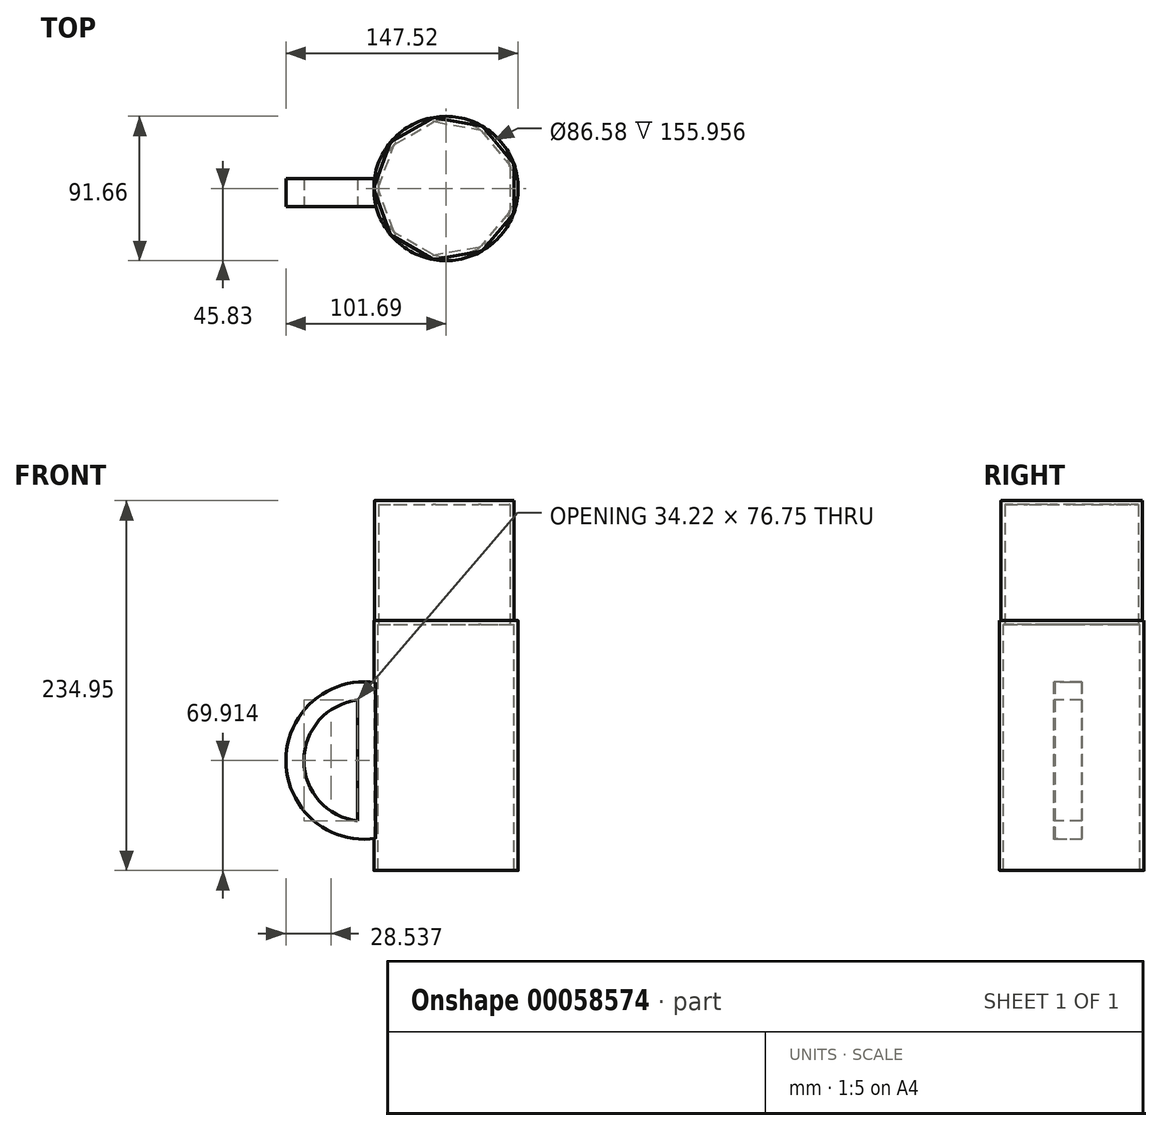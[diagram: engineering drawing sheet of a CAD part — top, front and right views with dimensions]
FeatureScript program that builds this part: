
annotation { "Feature Type Name" : "Feature", "Feature Type Description" : "" }
export const myFeature = defineFeature(function(context is Context, id is Id, definition is map)
    precondition{}
    {
        {
            var Q0;
            Q0=qCreatedBy(makeId("Top.planeOp"),FACE);
            var sketch = newSketch(context, id + "F0", { "sketchPlane" : qUnion([Q0])});
            skCircle(sketch, "E0.cCircle", {"center": v(0, 0) * mm, "radius": 43.07 * mm, "construction": true});
            skLineSegment(sketch, "E0.0", {"start": v(43.07, 15.68) * mm, "end": v(43.07, -15.68) * mm});
            skLineSegment(sketch, "E0.1", {"start": v(43.07, -15.68) * mm, "end": v(22.92, -39.7) * mm});
            skLineSegment(sketch, "E0.2", {"start": v(22.92, -39.7) * mm, "end": v(-7.96, -45.14) * mm});
            skLineSegment(sketch, "E0.3", {"start": v(-7.96, -45.14) * mm, "end": v(-35.1, -29.46) * mm});
            skLineSegment(sketch, "E0.4", {"start": v(-35.1, -29.46) * mm, "end": v(-45.83, 0) * mm});
            skLineSegment(sketch, "E0.5", {"start": v(-45.83, 0) * mm, "end": v(-35.1, 29.46) * mm});
            skLineSegment(sketch, "E0.6", {"start": v(-35.1, 29.46) * mm, "end": v(-7.96, 45.14) * mm});
            skLineSegment(sketch, "E0.7", {"start": v(-7.96, 45.14) * mm, "end": v(22.92, 39.7) * mm});
            skLineSegment(sketch, "E0.8", {"start": v(22.92, 39.7) * mm, "end": v(43.07, 15.68) * mm});
            skPoint(sketch, "E0.0.midPoint", {"position": v(43.07, 0) * mm});
            skSolve(sketch);
        }
        {
            var Q0;
            Q0 = qSketchRegion(id + "F0", true);
            extrude(context, id + "F1", {"entities" : qUnion([Q0]), "depth" : 76.2 * mm});
        }
        {
            var Q0;
            Q0=makeQuery(id+"F1.opExtrude","CAP_FACE",FACE,{"disambiguationData":[OSD([sQuery(id+"F0.wireOp",EDGE,"E0.0"),sQuery(id+"F0.wireOp",EDGE,"E0.1"),sQuery(id+"F0.wireOp",EDGE,"E0.2"),sQuery(id+"F0.wireOp",EDGE,"E0.3"),sQuery(id+"F0.wireOp",EDGE,"E0.4"),sQuery(id+"F0.wireOp",EDGE,"E0.5"),sQuery(id+"F0.wireOp",EDGE,"E0.6"),sQuery(id+"F0.wireOp",EDGE,"E0.7"),sQuery(id+"F0.wireOp",EDGE,"E0.8")])],"isStart":true});
            var sketch = newSketch(context, id + "F2", { "sketchPlane" : qUnion([Q0])});
            skCircle(sketch, "E1", {"center": v(0, 0) * mm, "radius": 45.83 * mm});
            skSolve(sketch);
        }
        {
            var Q0;
            Q0 = qSketchRegion(id + "F2", true);
            extrude(context, id + "F3", {"entities" : qUnion([Q0]), "operationType" : NewBodyOperationType.ADD, "depth" : 158.75 * mm});
        }
        {
            var Q0;
            Q0=makeQuery(id+"F1.opExtrude","SWEPT_EDGE",EDGE,{"disambiguationData":[OSD([sQuery(id+"F0.wireOp",EDGE,"E0.1"),sQuery(id+"F0.wireOp",EDGE,"E0.2")])]});
            var Q1;
            Q1=makeQuery(id+"F1.opExtrude","SWEPT_EDGE",EDGE,{"disambiguationData":[OSD([sQuery(id+"F0.wireOp",EDGE,"E0.0"),sQuery(id+"F0.wireOp",EDGE,"E0.1")])]});
            var Q2;
            Q2=makeQuery(id+"F1.opExtrude","SWEPT_EDGE",EDGE,{"disambiguationData":[OSD([sQuery(id+"F0.wireOp",EDGE,"E0.0"),sQuery(id+"F0.wireOp",EDGE,"E0.8")])]});
            var Q3;
            Q3=makeQuery(id+"F1.opExtrude","SWEPT_EDGE",EDGE,{"disambiguationData":[OSD([sQuery(id+"F0.wireOp",EDGE,"E0.7"),sQuery(id+"F0.wireOp",EDGE,"E0.8")])]});
            var Q4;
            Q4=makeQuery(id+"F1.opExtrude","SWEPT_EDGE",EDGE,{"disambiguationData":[OSD([sQuery(id+"F0.wireOp",EDGE,"E0.6"),sQuery(id+"F0.wireOp",EDGE,"E0.7")])]});
            var Q5;
            Q5=makeQuery(id+"F1.opExtrude","SWEPT_EDGE",EDGE,{"disambiguationData":[OSD([sQuery(id+"F0.wireOp",EDGE,"E0.5"),sQuery(id+"F0.wireOp",EDGE,"E0.6")])]});
            var Q6;
            Q6=makeQuery(id+"F1.opExtrude","SWEPT_EDGE",EDGE,{"disambiguationData":[OSD([sQuery(id+"F0.wireOp",EDGE,"E0.4"),sQuery(id+"F0.wireOp",EDGE,"E0.5")])]});
            var Q7;
            Q7=makeQuery(id+"F1.opExtrude","SWEPT_EDGE",EDGE,{"disambiguationData":[OSD([sQuery(id+"F0.wireOp",EDGE,"E0.3"),sQuery(id+"F0.wireOp",EDGE,"E0.4")])]});
            var Q8;
            Q8=makeQuery(id+"F1.opExtrude","SWEPT_EDGE",EDGE,{"disambiguationData":[OSD([sQuery(id+"F0.wireOp",EDGE,"E0.2"),sQuery(id+"F0.wireOp",EDGE,"E0.3")])]});
            fillet(context, id + "F4", {"entities" : qUnion([Q0, Q1, Q2, Q3, Q4, Q5, Q6, Q7, Q8]), "radius" : 5.08 * mm, "tangentPropagation" : true, "allowEdgeOverflow" : false});
        }
        {
            var Q0;
            Q0=makeQuery(id+"F3.opExtrude","CAP_FACE",FACE,{"disambiguationData":[OSD([sQuery(id+"F2.wireOp",EDGE,"E1")])],"isStart":false});
            shell(context, id + "F5", {"entities" : qUnion([Q0]), "thickness" : 2.54 * mm});
        }
        {
            var Q0;
            {var subQ0=sQuery(id+"F2.wireOp",EDGE,"E1");Q0=makeQuery(id+"F5.opShell","OFFSET_EDGE",EDGE,{"disambiguationData":[OSD([subQ0]),TDD([makeQuery(id+"F3.opExtrude","CAP_EDGE",EDGE,{"disambiguationData":[OSD([subQ0])],"isStart":false})])]});}
            var Q1;
            Q1=makeQuery(id+"F3.opExtrude","CAP_EDGE",EDGE,{"disambiguationData":[OSD([sQuery(id+"F2.wireOp",EDGE,"E1")])],"isStart":false});
            fillet(context, id + "F6", {"entities" : qUnion([Q0, Q1]), "radius" : 0.25 * mm, "tangentPropagation" : true, "allowEdgeOverflow" : false});
        }
        {
            var Q0;
            Q0=qCreatedBy(makeId("Front.planeOp"),FACE);
            cPlane(context, id + "F7", {"entities" : qUnion([Q0]), "cplaneType" : CPlaneType.OFFSET, "offset" : 11.43 * mm, "width" : 152.4 * mm, "height" : 152.4 * mm});
        }
        {
            var Q0;
            Q0=qCreatedBy(id+"F7.planeOp",FACE);
            var sketch = newSketch(context, id + "F8", { "sketchPlane" : qUnion([Q0])});
            skLineSegment(sketch, "E2", {"start": v(-44.61, -138.4) * mm, "end": v(-44.61, -39.27) * mm});
            skArc(sketch, "E3", {"start": v(-44.61, -39.27) * mm, "mid": v(-101.7, -88.84) * mm, "end": v(-44.61, -138.4) * mm});
            skArc(sketch, "E4.0", {"start": v(-56.04, -50.46) * mm, "mid": v(-90.26, -88.84) * mm, "end": v(-56.04, -127.21) * mm});
            skLineSegment(sketch, "E4.1", {"start": v(-56.04, -127.21) * mm, "end": v(-56.04, -50.46) * mm});
            skSolve(sketch);
        }
        {
            var Q0;
            Q0 = qSketchRegion(id + "F8", true);
            extrude(context, id + "F9", {"entities" : qUnion([Q0]), "operationType" : NewBodyOperationType.ADD, "oppositeDirection" : true, "depth" : 17.78 * mm});
        }
    });
